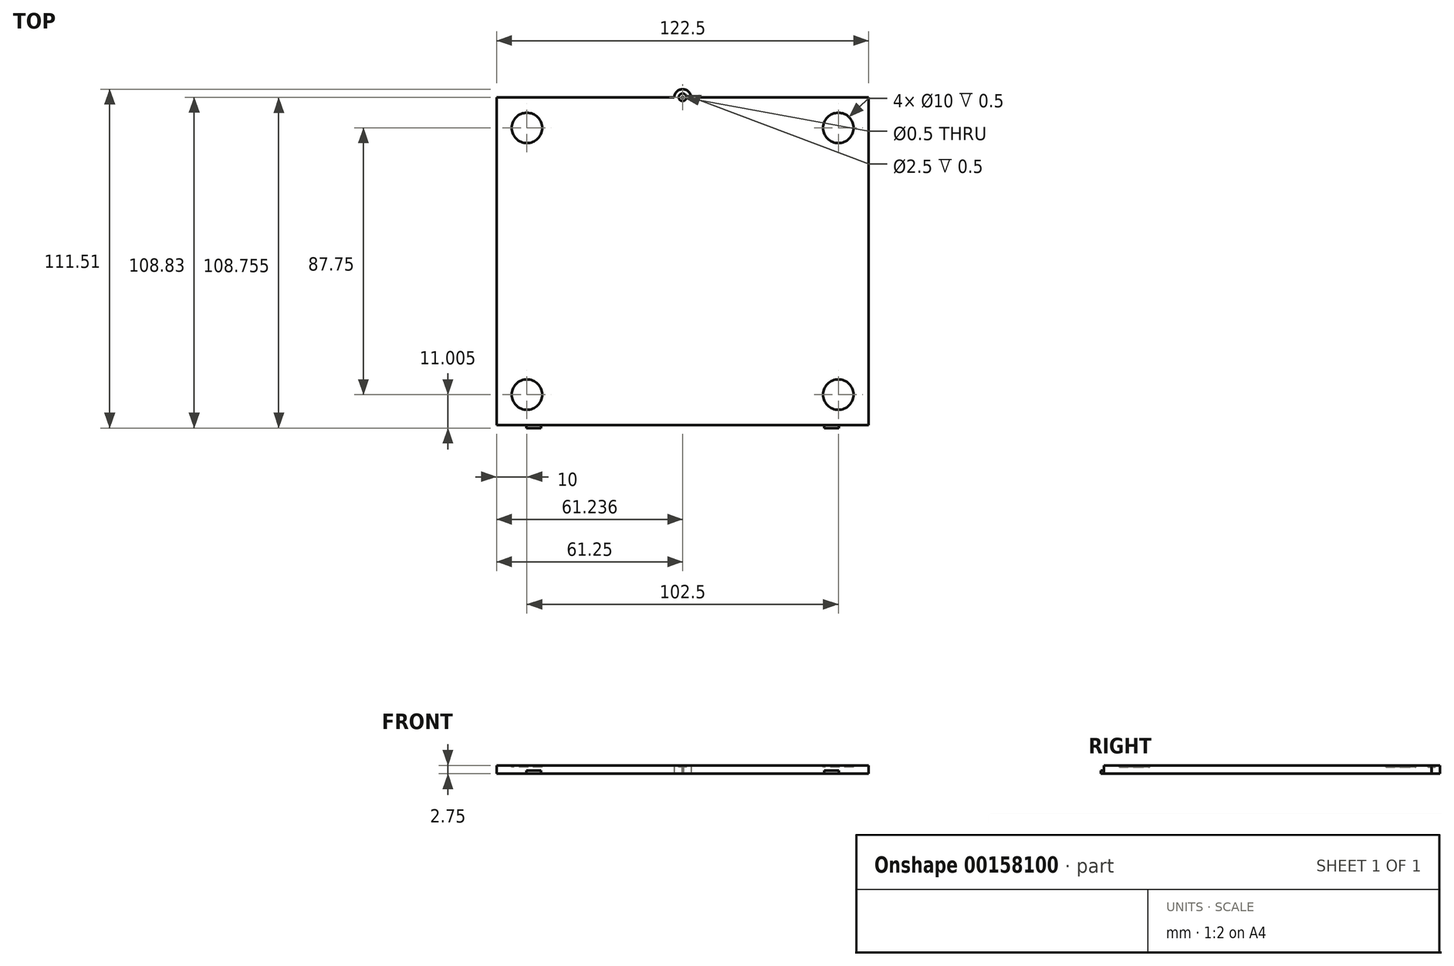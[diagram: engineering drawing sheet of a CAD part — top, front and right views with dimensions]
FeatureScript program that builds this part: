
annotation { "Feature Type Name" : "Feature", "Feature Type Description" : "" }
export const myFeature = defineFeature(function(context is Context, id is Id, definition is map)
    precondition{}
    {
        {
            var Q0;
            Q0=qCreatedBy(makeId("Top.planeOp"),FACE);
            var sketch = newSketch(context, id + "F0", { "sketchPlane" : qUnion([Q0])});
            skLineSegment(sketch, "E0.bottom", {"start": v(61.25, 53.87) * mm, "end": v(-61.25, 53.87) * mm});
            skLineSegment(sketch, "E0.top", {"start": v(61.25, -53.88) * mm, "end": v(-61.25, -53.88) * mm});
            skLineSegment(sketch, "E0.left", {"start": v(61.25, 53.87) * mm, "end": v(61.25, -53.88) * mm});
            skLineSegment(sketch, "E0.right", {"start": v(-61.25, 53.87) * mm, "end": v(-61.25, -53.88) * mm});
            skPoint(sketch, "E0.middle", {"position": v(0, 0) * mm});
            skArc(sketch, "E1", {"start": v(2.75, 53.87) * mm, "mid": v(0, 56.63) * mm, "end": v(-2.75, 53.87) * mm});
            skSolve(sketch);
        }
        {
            var Q0;
            Q0 = qSketchRegion(id + "F0", true);
            extrude(context, id + "F1", {"entities" : qUnion([Q0]), "depth" : 2.75 * mm});
        }
        {
            var Q0;
            Q0=makeQuery(id+"F1.opExtrude","SWEPT_FACE",FACE,{"disambiguationData":[OSD([sQuery(id+"F0.wireOp",EDGE,"E0.top")])]});
            var sketch = newSketch(context, id + "F2", { "sketchPlane" : qUnion([Q0])});
            skLineSegment(sketch, "E2.bottom", {"start": v(-51.37, 0) * mm, "end": v(-46.62, 0) * mm});
            skLineSegment(sketch, "E2.top", {"start": v(-51.37, 1) * mm, "end": v(-46.62, 1) * mm});
            skLineSegment(sketch, "E2.left", {"start": v(-51.37, 0) * mm, "end": v(-51.37, 1) * mm});
            skLineSegment(sketch, "E2.right", {"start": v(-46.62, 0) * mm, "end": v(-46.62, 1) * mm});
            skLineSegment(sketch, "E3.bottom", {"start": v(51.38, 0) * mm, "end": v(46.62, 0) * mm});
            skLineSegment(sketch, "E3.top", {"start": v(51.38, 1) * mm, "end": v(46.62, 1) * mm});
            skLineSegment(sketch, "E3.left", {"start": v(51.38, 0) * mm, "end": v(51.38, 1) * mm});
            skLineSegment(sketch, "E3.right", {"start": v(46.62, 0) * mm, "end": v(46.62, 1) * mm});
            skSolve(sketch);
        }
        {
            var Q0;
            Q0=makeQuery(id+"F2.imprint","IMPRINT",FACE,{"disambiguationData":[TD([[makeQuery(id+"F2.imprint","IMPRINT",EDGE,{"derivedFrom":sQuery(id+"F2.wireOp",EDGE,"E2.bottom")}),-1.0]])]});
            var Q1;
            Q1=makeQuery(id+"F2.imprint","IMPRINT",FACE,{"disambiguationData":[TD([[makeQuery(id+"F2.imprint","IMPRINT",EDGE,{"derivedFrom":sQuery(id+"F2.wireOp",EDGE,"E3.bottom")}),-1.0]])]});
            extrude(context, id + "F3", {"entities" : qUnion([Q0, Q1]), "operationType" : NewBodyOperationType.ADD, "depth" : 1 * mm});
        }
        {
            var Q0;
            Q0=sQuery(id+"F0.wireOp",VERTEX,"E1.center");
            var Q1;
            Q1=makeQuery(id+"F1.opExtrude","SWEPT_BODY",BODY,{"disambiguationData":[OSD([sQuery(id+"F0.wireOp",EDGE,"E0.bottom"),sQuery(id+"F0.wireOp",EDGE,"E0.top"),sQuery(id+"F0.wireOp",EDGE,"E0.left"),sQuery(id+"F0.wireOp",EDGE,"E0.right"),sQuery(id+"F0.wireOp",EDGE,"E1")])]});
            hole(context, id + "F4", {"style" : HoleStyle.SIMPLE, "endStyle" : HoleEndStyle.BLIND, "oppositeDirection" : true, "holeDiameter" : .5 * mm, "holeDepth" : 2.75 * mm, "startFromSketch" : true, "locations" : qUnion([Q0]), "scope" : qUnion([Q1])});
        }
        {
            var Q0;
            Q0=makeQuery(id+"F1.opExtrude","CAP_FACE",FACE,{"disambiguationData":[OSD([sQuery(id+"F0.wireOp",EDGE,"E0.bottom"),sQuery(id+"F0.wireOp",EDGE,"E0.top"),sQuery(id+"F0.wireOp",EDGE,"E0.left"),sQuery(id+"F0.wireOp",EDGE,"E0.right"),sQuery(id+"F0.wireOp",EDGE,"E1")])],"isStart":false});
            var sketch = newSketch(context, id + "F5", { "sketchPlane" : qUnion([Q0])});
            skCircle(sketch, "E4", {"center": v(51.25, 43.87) * mm, "radius": 5 * mm});
            skCircle(sketch, "E5", {"center": v(-51.25, 43.88) * mm, "radius": 5 * mm});
            skCircle(sketch, "E6", {"center": v(-51.25, -43.88) * mm, "radius": 5 * mm});
            skCircle(sketch, "E7", {"center": v(51.25, -43.88) * mm, "radius": 5 * mm});
            skCircle(sketch, "E8", {"center": v(-0.01, 53.95) * mm, "radius": 1.25 * mm});
            skPoint(sketch, "E8.first.point", {"position": v(0, 55.2) * mm});
            skPoint(sketch, "E8.second.point", {"position": v(0, 52.7) * mm});
            skPoint(sketch, "E8.second.point.positionSnap0", {"position": v(0, 56.63) * mm});
            skPoint(sketch, "E8.third.point", {"position": v(1.22, 54.13) * mm});
            skSolve(sketch);
        }
        {
            var Q0;
            Q0=makeQuery(id+"F5.imprint","IMPRINT",FACE,{"disambiguationData":[TD([[makeQuery(id+"F5.imprint","IMPRINT",EDGE,{"derivedFrom":sQuery(id+"F5.wireOp",EDGE,"E4")}),1.0]])]});
            var Q1;
            Q1=makeQuery(id+"F5.imprint","IMPRINT",FACE,{"disambiguationData":[TD([[makeQuery(id+"F5.imprint","IMPRINT",EDGE,{"derivedFrom":sQuery(id+"F5.wireOp",EDGE,"E8")}),1.0]])]});
            var Q2;
            Q2=makeQuery(id+"F5.imprint","IMPRINT",FACE,{"disambiguationData":[TD([[makeQuery(id+"F5.imprint","IMPRINT",EDGE,{"derivedFrom":sQuery(id+"F5.wireOp",EDGE,"E5")}),1.0]])]});
            var Q3;
            Q3=makeQuery(id+"F5.imprint","IMPRINT",FACE,{"disambiguationData":[TD([[makeQuery(id+"F5.imprint","IMPRINT",EDGE,{"derivedFrom":sQuery(id+"F5.wireOp",EDGE,"E7")}),1.0]])]});
            var Q4;
            Q4=makeQuery(id+"F5.imprint","IMPRINT",FACE,{"disambiguationData":[TD([[makeQuery(id+"F5.imprint","IMPRINT",EDGE,{"derivedFrom":sQuery(id+"F5.wireOp",EDGE,"E6")}),1.0]])]});
            extrude(context, id + "F6", {"entities" : qUnion([Q0, Q1, Q2, Q3, Q4]), "operationType" : NewBodyOperationType.REMOVE, "oppositeDirection" : true, "depth" : .5 * mm});
        }
    });
